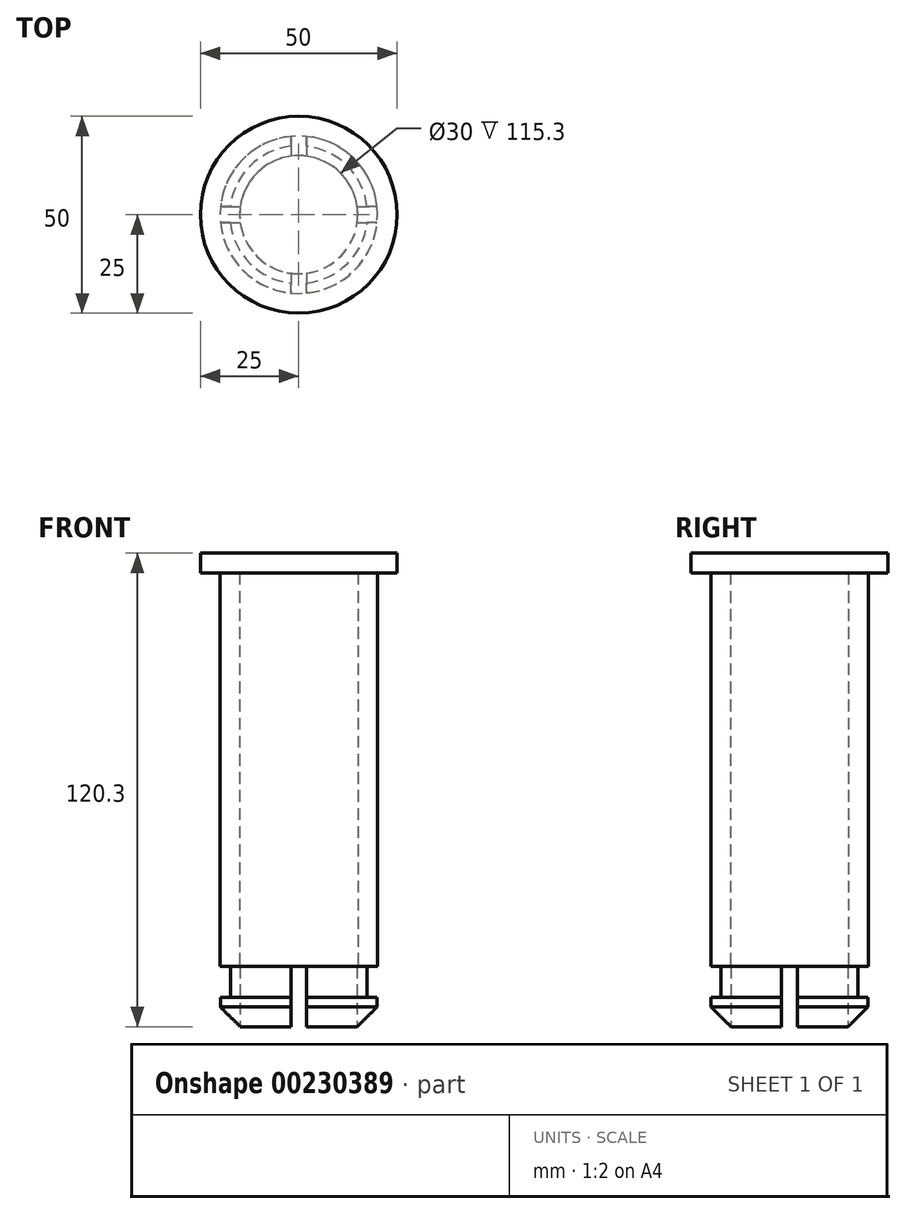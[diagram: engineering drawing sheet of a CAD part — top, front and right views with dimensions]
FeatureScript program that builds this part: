
annotation { "Feature Type Name" : "Feature", "Feature Type Description" : "" }
export const myFeature = defineFeature(function(context is Context, id is Id, definition is map)
    precondition{}
    {
        {
            var Q0;
            Q0=qCreatedBy(makeId("Top.planeOp"),FACE);
            var sketch = newSketch(context, id + "F0", { "sketchPlane" : qUnion([Q0])});
            skCircle(sketch, "E0", {"center": v(0, 0) * mm, "radius": 20 * mm});
            skSolve(sketch);
        }
        {
            var Q0;
            Q0 = qSketchRegion(id + "F0", true);
            extrude(context, id + "F1", {"entities" : qUnion([Q0]), "depth" : 7.5 * mm});
        }
        {
            var Q0;
            Q0=makeQuery(id+"F1.opExtrude","CAP_FACE",FACE,{"disambiguationData":[OSD([sQuery(id+"F0.wireOp",EDGE,"E0")])],"isStart":false});
            var sketch = newSketch(context, id + "F2", { "sketchPlane" : qUnion([Q0])});
            skCircle(sketch, "E1", {"center": v(0, 0) * mm, "radius": 17.5 * mm});
            skSolve(sketch);
        }
        {
            var Q0;
            Q0 = qSketchRegion(id + "F2", true);
            extrude(context, id + "F3", {"entities" : qUnion([Q0]), "operationType" : NewBodyOperationType.ADD, "depth" : 7.8 * mm});
        }
        {
            var Q0;
            Q0=makeQuery(id+"F3.opExtrude","CAP_FACE",FACE,{"disambiguationData":[OSD([sQuery(id+"F2.wireOp",EDGE,"E1")])],"isStart":false});
            var sketch = newSketch(context, id + "F4", { "sketchPlane" : qUnion([Q0])});
            skCircle(sketch, "E2", {"center": v(0, 0) * mm, "radius": 20 * mm});
            skSolve(sketch);
        }
        {
            var Q0;
            Q0 = qSketchRegion(id + "F4", true);
            extrude(context, id + "F5", {"entities" : qUnion([Q0]), "operationType" : NewBodyOperationType.ADD, "depth" : 100 * mm});
        }
        {
            var Q0;
            Q0=makeQuery(id+"F5.opExtrude","CAP_FACE",FACE,{"disambiguationData":[OSD([sQuery(id+"F4.wireOp",EDGE,"E2")])],"isStart":false});
            var sketch = newSketch(context, id + "F6", { "sketchPlane" : qUnion([Q0])});
            skCircle(sketch, "E3", {"center": v(0, 0) * mm, "radius": 25 * mm});
            skSolve(sketch);
        }
        {
            var Q0;
            Q0 = qSketchRegion(id + "F6", true);
            extrude(context, id + "F7", {"entities" : qUnion([Q0]), "operationType" : NewBodyOperationType.ADD, "depth" : 5 * mm});
        }
        {
            var Q0;
            Q0=makeQuery(id+"F1.opExtrude","CAP_EDGE",EDGE,{"disambiguationData":[OSD([sQuery(id+"F0.wireOp",EDGE,"E0")])],"isStart":true});
            chamfer(context, id + "F8", {"entities" : qUnion([Q0]), "width" : 5 * mm, "tangentPropagation" : true});
        }
        {
            var Q0;
            Q0=makeQuery(id+"F1.opExtrude","CAP_FACE",FACE,{"disambiguationData":[OSD([sQuery(id+"F0.wireOp",EDGE,"E0")])],"isStart":true});
            var sketch = newSketch(context, id + "F9", { "sketchPlane" : qUnion([Q0])});
            skCircle(sketch, "E4", {"center": v(0, 0) * mm, "radius": 15 * mm});
            skSolve(sketch);
        }
        {
            var Q0;
            Q0 = qSketchRegion(id + "F9", true);
            var Q1;
            Q1=makeQuery(id+"F7.opExtrude","CAP_FACE",FACE,{"disambiguationData":[OSD([sQuery(id+"F6.wireOp",EDGE,"E3")])],"isStart":true});
            extrude(context, id + "F10", {"entities" : qUnion([Q0]), "operationType" : NewBodyOperationType.REMOVE, "endBound" : BoundingType.UP_TO_SURFACE, "oppositeDirection" : true, "endBoundEntityFace" : qUnion([Q1]), "depth" : 87.5 * mm});
        }
        {
            var Q0;
            Q0=qCreatedBy(makeId("Front.planeOp"),FACE);
            var sketch = newSketch(context, id + "F11", { "sketchPlane" : qUnion([Q0])});
            skLineSegment(sketch, "E5.0", {"start": v(-20, 15.3) * mm, "end": v(20, 15.3) * mm, "construction": true});
            skLineSegment(sketch, "E6.0", {"start": v(15, 0) * mm, "end": v(-15, 0) * mm, "construction": true});
            skLineSegment(sketch, "E7.bottom", {"start": v(-2, 0) * mm, "end": v(2, 0) * mm});
            skLineSegment(sketch, "E7.top", {"start": v(-2, 15.3) * mm, "end": v(2, 15.3) * mm});
            skLineSegment(sketch, "E7.left", {"start": v(-2, 0) * mm, "end": v(-2, 15.3) * mm});
            skLineSegment(sketch, "E7.right", {"start": v(2, 0) * mm, "end": v(2, 15.3) * mm});
            skSolve(sketch);
        }
        {
            var Q0;
            Q0 = qSketchRegion(id + "F11", true);
            extrude(context, id + "F12", {"entities" : qUnion([Q0]), "operationType" : NewBodyOperationType.REMOVE, "endBound" : BoundingType.SYMMETRIC, "oppositeDirection" : true, "depth" : 50 * mm});
        }
        {
            var Q0;
            Q0=qCreatedBy(makeId("Right.planeOp"),FACE);
            var sketch = newSketch(context, id + "F13", { "sketchPlane" : qUnion([Q0])});
            skLineSegment(sketch, "E8.0", {"start": v(-20, 15.3) * mm, "end": v(20, 15.3) * mm, "construction": true});
            skLineSegment(sketch, "E9.0", {"start": v(15, 0) * mm, "end": v(-15, 0) * mm, "construction": true});
            skLineSegment(sketch, "E10.bottom", {"start": v(-2, 0) * mm, "end": v(2, 0) * mm});
            skLineSegment(sketch, "E10.top", {"start": v(-2, 15.3) * mm, "end": v(2, 15.3) * mm});
            skLineSegment(sketch, "E10.left", {"start": v(-2, 0) * mm, "end": v(-2, 15.3) * mm});
            skLineSegment(sketch, "E10.right", {"start": v(2, 0) * mm, "end": v(2, 15.3) * mm});
            skSolve(sketch);
        }
        {
            var Q0;
            Q0 = qSketchRegion(id + "F13", true);
            extrude(context, id + "F14", {"entities" : qUnion([Q0]), "operationType" : NewBodyOperationType.REMOVE, "endBound" : BoundingType.SYMMETRIC, "oppositeDirection" : true, "depth" : 50 * mm});
        }
    });
